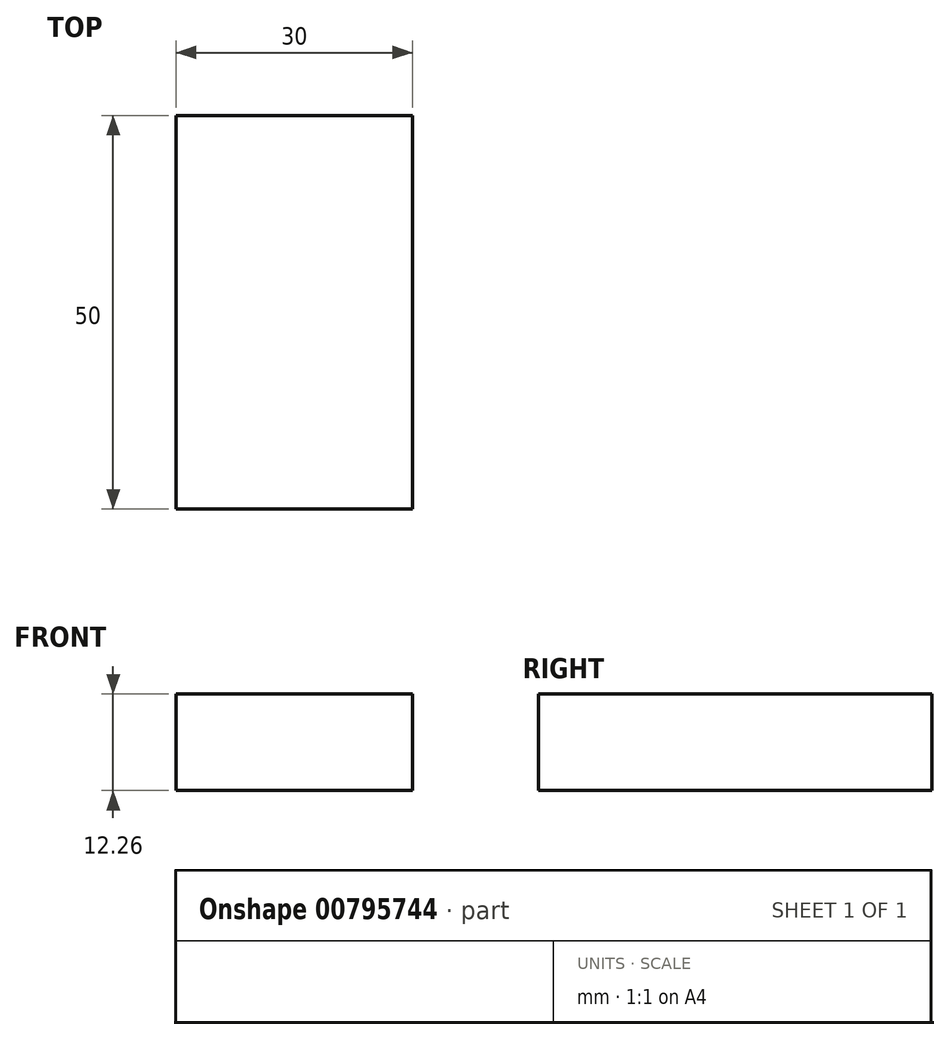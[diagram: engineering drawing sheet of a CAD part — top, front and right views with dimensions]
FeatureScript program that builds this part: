
annotation { "Feature Type Name" : "Feature", "Feature Type Description" : "" }
export const myFeature = defineFeature(function(context is Context, id is Id, definition is map)
    precondition{}
    {
        {
            var Q0;
            Q0=qCreatedBy(makeId("Front.planeOp"),FACE);
            var sketch = newSketch(context, id + "F0", { "sketchPlane" : qUnion([Q0])});
            skLineSegment(sketch, "E0.bottom", {"start": v(15, -6.13) * mm, "end": v(-15, -6.13) * mm});
            skLineSegment(sketch, "E0.top", {"start": v(15, 6.13) * mm, "end": v(-15, 6.13) * mm});
            skLineSegment(sketch, "E0.left", {"start": v(15, -6.13) * mm, "end": v(15, 6.13) * mm});
            skLineSegment(sketch, "E0.right", {"start": v(-15, -6.13) * mm, "end": v(-15, 6.13) * mm});
            skPoint(sketch, "E0.middle", {"position": v(0, 0) * mm});
            skSolve(sketch);
        }
        {
            var Q0;
            Q0 = qSketchRegion(id + "F0", true);
            extrude(context, id + "F1", {"entities" : qUnion([Q0]), "depth" : 50 * mm, "offsetDistance" : 25 * mm});
        }
    });
